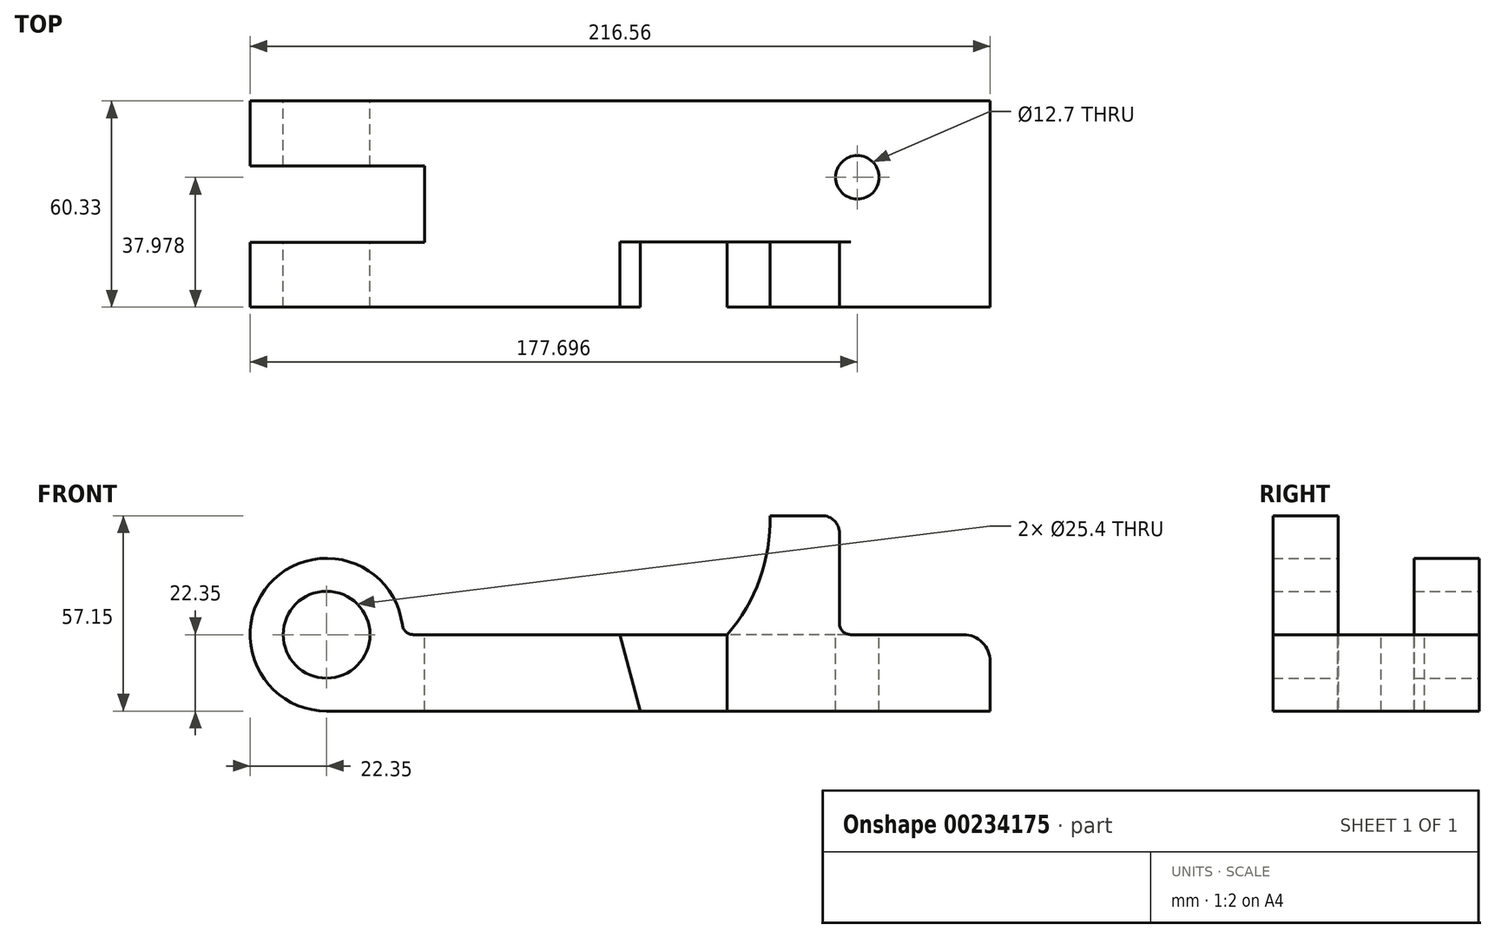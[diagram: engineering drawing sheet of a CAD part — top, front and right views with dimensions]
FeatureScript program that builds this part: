
annotation { "Feature Type Name" : "Feature", "Feature Type Description" : "" }
export const myFeature = defineFeature(function(context is Context, id is Id, definition is map)
    precondition{}
    {
        {
            var Q0;
            Q0=qCreatedBy(makeId("Front.planeOp"),FACE);
            var sketch = newSketch(context, id + "F0", { "sketchPlane" : qUnion([Q0])});
            skArc(sketch, "E0", {"start": v(22.35, 0) * mm, "mid": v(-15.8, 15.8) * mm, "end": v(0, -22.35) * mm});
            skCircle(sketch, "E1", {"center": v(0, 0) * mm, "radius": 12.7 * mm});
            skLineSegment(sketch, "E2", {"start": v(22.35, 0) * mm, "end": v(117.25, 0) * mm});
            skLineSegment(sketch, "E3", {"start": v(129.77, 34.8) * mm, "end": v(150.09, 34.8) * mm});
            skLineSegment(sketch, "E4", {"start": v(150.09, 34.8) * mm, "end": v(150.09, 0) * mm});
            skLineSegment(sketch, "E5", {"start": v(150.09, 0) * mm, "end": v(194.2, 0) * mm});
            skLineSegment(sketch, "E6", {"start": v(0, -22.35) * mm, "end": v(194.2, -22.35) * mm});
            skLineSegment(sketch, "E7", {"start": v(194.2, -22.35) * mm, "end": v(194.2, 0) * mm});
            skArc(sketch, "E8", {"start": v(117.25, 0) * mm, "mid": v(126.79, 16.22) * mm, "end": v(129.77, 34.8) * mm});
            skSolve(sketch);
        }
        {
            var Q0;
            Q0=qSketchRegion(id+"F0",true);
            extrude(context, id + "F1", {"entities" : qUnion([Q0]), "depth" : 60.32 * mm});
        }
        {
            var Q0;
            Q0=makeQuery(id+"F1.opExtrude","SWEPT_EDGE",EDGE,{"disambiguationData":[OSD([sQuery(id+"F0.wireOp",EDGE,"E0"),sQuery(id+"F0.wireOp",EDGE,"E2")])]});
            var Q1;
            Q1=makeQuery(id+"F1.opExtrude","SWEPT_EDGE",EDGE,{"disambiguationData":[OSD([sQuery(id+"F0.wireOp",EDGE,"E4"),sQuery(id+"F0.wireOp",EDGE,"E5")])]});
            fillet(context, id + "F2", {"entities" : qUnion([Q0, Q1]), "radius" : 3.3 * mm, "tangentPropagation" : true, "allowEdgeOverflow" : false});
        }
        {
            var Q0;
            Q0=makeQuery(id+"F1.opExtrude","SWEPT_FACE",FACE,{"disambiguationData":[OSD([sQuery(id+"F0.wireOp",EDGE,"E3")])]});
            var sketch = newSketch(context, id + "F3", { "sketchPlane" : qUnion([Q0])});
            skLineSegment(sketch, "E9.bottom", {"start": v(-28.74, -19) * mm, "end": v(28.74, -19) * mm});
            skLineSegment(sketch, "E9.top", {"start": v(-28.74, -41.33) * mm, "end": v(28.74, -41.33) * mm});
            skLineSegment(sketch, "E9.left", {"start": v(-28.74, -19) * mm, "end": v(-28.74, -41.33) * mm});
            skLineSegment(sketch, "E9.right", {"start": v(28.74, -19) * mm, "end": v(28.74, -41.33) * mm});
            skPoint(sketch, "E9.middle", {"position": v(0, -30.16) * mm});
            skLineSegment(sketch, "E10.bottom", {"start": v(106.92, -41.28) * mm, "end": v(163.55, -41.28) * mm});
            skLineSegment(sketch, "E10.top", {"start": v(106.92, 0) * mm, "end": v(163.55, 0) * mm});
            skLineSegment(sketch, "E10.left", {"start": v(106.92, -41.28) * mm, "end": v(106.92, 0) * mm});
            skLineSegment(sketch, "E10.right", {"start": v(163.55, -41.28) * mm, "end": v(163.55, 0) * mm});
            skSolve(sketch);
        }
        {
            var Q0;
            Q0=makeQuery(id+"F3.imprint","IMPRINT",FACE,{"disambiguationData":[TD([[makeQuery(id+"F3.imprint","IMPRINT",EDGE,{"derivedFrom":sQuery(id+"F3.wireOp",EDGE,"E9.bottom")}),-1.0]])]});
            extrude(context, id + "F4", {"entities" : qUnion([Q0]), "operationType" : NewBodyOperationType.REMOVE, "endBound" : BoundingType.THROUGH_ALL, "oppositeDirection" : true, "depth" : 25.4 * mm});
        }
        {
            var Q0;
            {var subQ0=sQuery(id+"F3.wireOp",EDGE,"E10.left");Q0=makeQuery(id+"F3.imprint","IMPRINT",FACE,{"disambiguationData":[TD([[makeQuery(id+"F3.imprint","IMPRINT",EDGE,{"derivedFrom":subQ0}),-1.0]])]});}
            var Q1;
            {var subQ0=sQuery(id+"F3.wireOp",EDGE,"E10.bottom");var subQ1=sQuery(id+"F0.wireOp",EDGE,"E3");var subQ2=makeQuery(id+"F1.opExtrude","SWEPT_EDGE",EDGE,{"disambiguationData":[OSD([subQ1,sQuery(id+"F0.wireOp",EDGE,"E8")])]});var subQ3=makeQuery(id+"F3.imprint","INTERSECT",VERTEX,{"derivedFrom":[subQ2,subQ0]});Q1=makeQuery(id+"F3.imprint","IMPRINT",FACE,{"disambiguationData":[TD([[makeQuery(id+"F3.imprint","IMPRINT",EDGE,{"disambiguationData":[TD([[subQ3,-1.0]])],"derivedFrom":subQ0}),1.0]])]});}
            var Q2;
            {var subQ0=sQuery(id+"F3.wireOp",EDGE,"E10.right");Q2=makeQuery(id+"F3.imprint","IMPRINT",FACE,{"disambiguationData":[TD([[makeQuery(id+"F3.imprint","IMPRINT",EDGE,{"derivedFrom":subQ0}),1.0]])]});}
            var Q3;
            Q3=makeQuery(id+"F1.opExtrude","SWEPT_FACE",FACE,{"disambiguationData":[OSD([sQuery(id+"F0.wireOp",EDGE,"E5")])]});
            extrude(context, id + "F5", {"entities" : qUnion([Q0, Q1, Q2]), "operationType" : NewBodyOperationType.REMOVE, "endBound" : BoundingType.UP_TO_SURFACE, "oppositeDirection" : true, "endBoundEntityFace" : qUnion([Q3]), "depth" : 25.4 * mm});
        }
        {
            var Q0;
            {var subQ0=sQuery(id+"F0.wireOp",EDGE,"E5");Q0=makeQuery(id+"F5.boolean.opBoolean","MERGE",FACE,{"derivedFrom":[makeQuery(id+"F1.opExtrude","SWEPT_FACE",FACE,{"disambiguationData":[OSD([subQ0])]}),makeQuery(id+"F1.opExtrude","SWEPT_FACE",FACE,{"disambiguationData":[OSD([sQuery(id+"F0.wireOp",EDGE,"E2")])]}),makeQuery(id+"F5.opExtrude","CAP_FACE",FACE,{"disambiguationData":[OSD([subQ0])],"isStart":false})]});}
            var sketch = newSketch(context, id + "F6", { "sketchPlane" : qUnion([Q0])});
            skCircle(sketch, "E11", {"center": v(155.35, -22.35) * mm, "radius": 6.35 * mm});
            skSolve(sketch);
        }
        {
            var Q0;
            Q0=qSketchRegion(id+"F6",true);
            extrude(context, id + "F7", {"entities" : qUnion([Q0]), "operationType" : NewBodyOperationType.REMOVE, "endBound" : BoundingType.THROUGH_ALL, "oppositeDirection" : true, "depth" : 25.4 * mm});
        }
        {
            var Q0;
            Q0=makeQuery(id+"F1.opExtrude","SWEPT_EDGE",EDGE,{"disambiguationData":[OSD([sQuery(id+"F0.wireOp",EDGE,"E3"),sQuery(id+"F0.wireOp",EDGE,"E4")])]});
            fillet(context, id + "F8", {"entities" : qUnion([Q0]), "radius" : 5.08 * mm, "tangentPropagation" : true, "allowEdgeOverflow" : false});
        }
        {
            var Q0;
            Q0=makeQuery(id+"F1.opExtrude","SWEPT_EDGE",EDGE,{"disambiguationData":[OSD([sQuery(id+"F0.wireOp",EDGE,"E5"),sQuery(id+"F0.wireOp",EDGE,"E7")])]});
            fillet(context, id + "F9", {"entities" : qUnion([Q0]), "radius" : 7.87 * mm, "tangentPropagation" : true, "allowEdgeOverflow" : false});
        }
        {
            var Q0;
            Q0=makeQuery(id+"F1.opExtrude","CAP_FACE",FACE,{"disambiguationData":[OSD([sQuery(id+"F0.wireOp",EDGE,"E0"),sQuery(id+"F0.wireOp",EDGE,"E1"),sQuery(id+"F0.wireOp",EDGE,"E2"),sQuery(id+"F0.wireOp",EDGE,"E3"),sQuery(id+"F0.wireOp",EDGE,"E4"),sQuery(id+"F0.wireOp",EDGE,"E5"),sQuery(id+"F0.wireOp",EDGE,"E6"),sQuery(id+"F0.wireOp",EDGE,"E7"),sQuery(id+"F0.wireOp",EDGE,"E8")])],"isStart":false});
            var sketch = newSketch(context, id + "F10", { "sketchPlane" : qUnion([Q0])});
            skLineSegment(sketch, "E12", {"start": v(117.25, 0) * mm, "end": v(117.25, -22.35) * mm});
            skLineSegment(sketch, "E13", {"start": v(117.25, -22.35) * mm, "end": v(91.85, -22.35) * mm});
            skLineSegment(sketch, "E14", {"start": v(91.85, -22.35) * mm, "end": v(85.85, 0) * mm});
            skLineSegment(sketch, "E15", {"start": v(85.85, 0) * mm, "end": v(117.25, 0) * mm});
            skSolve(sketch);
        }
        {
            var Q0;
            Q0=qSketchRegion(id+"F10",true);
            extrude(context, id + "F11", {"entities" : qUnion([Q0]), "operationType" : NewBodyOperationType.REMOVE, "oppositeDirection" : true, "depth" : 19.05 * mm});
        }
    });
